# Revit family: QF_HOSHIZAKI_FM-120KE-HC
name_source: partatom
category: Specialty Equipment
revit_build: Autodesk Revit 2016 (Build: 20150220_1215(x64)
units: mm (PartAtom-declared; Revit-internal decimal feet)

## family parameters
Always vertical = Yes
Cut with Voids When Loaded = No
OmniClass Number = 23.40.40.14
OmniClass Title = Food Service Equipment
Part Type = Normal
Room Calculation Point = No
Round Connector Dimension = Use Diameter
Shared = No
Work Plane-Based = No

## types (2) — shared parameters
Accessory = No
Apparent Power = 355 VA
Assembly Code = E1090320
Cold Water Flow = 0.0 L/s
Cold Water Size = 19 mm
Cold Water Temperature Recommended = 0 °C
Conn Conduit = No
Depth Actual = 600 mm
Description = FM HYDROCARBON ICE MAKER, 125KG PER 24 HOURS, COUNTER, FLAKE
Electric power = 355 W
FL Amps = 20 A
Height Actual = 800 mm  [stored 2.62467 ft]
Indirect Waste Size = 19 mm
Length Actual = 640 mm  [stored 2.09974 ft]
Manufacturer = HOSHIZAKI
Max Overcurrent Protection = 0 A
Min Ckt Ampacity = 0 A
Model = FM-120KE-HC
Number of Poles = 2
Phase = 1
URL = www.hoshizaki-europe.com
Weight = 66.00 kg
zero-valued in all types: Cost

## per-type parameters (varying)
| type | Cycle | Volts |
| FM-120KE-HC_230V/1Ph/50Hz | 50 Hz | 230 V |
| FM-120KE-HC_240V/1Ph/60Hz | 60 Hz | 240 V |

note: [stored X ft] marks values corroborated as IEEE doubles in the binary element streams (Revit-internal decimal feet)

## geometry (parser evidence)
native form markers: Blend x2, Sweep x9
no freeform markers — native parametric forms only
